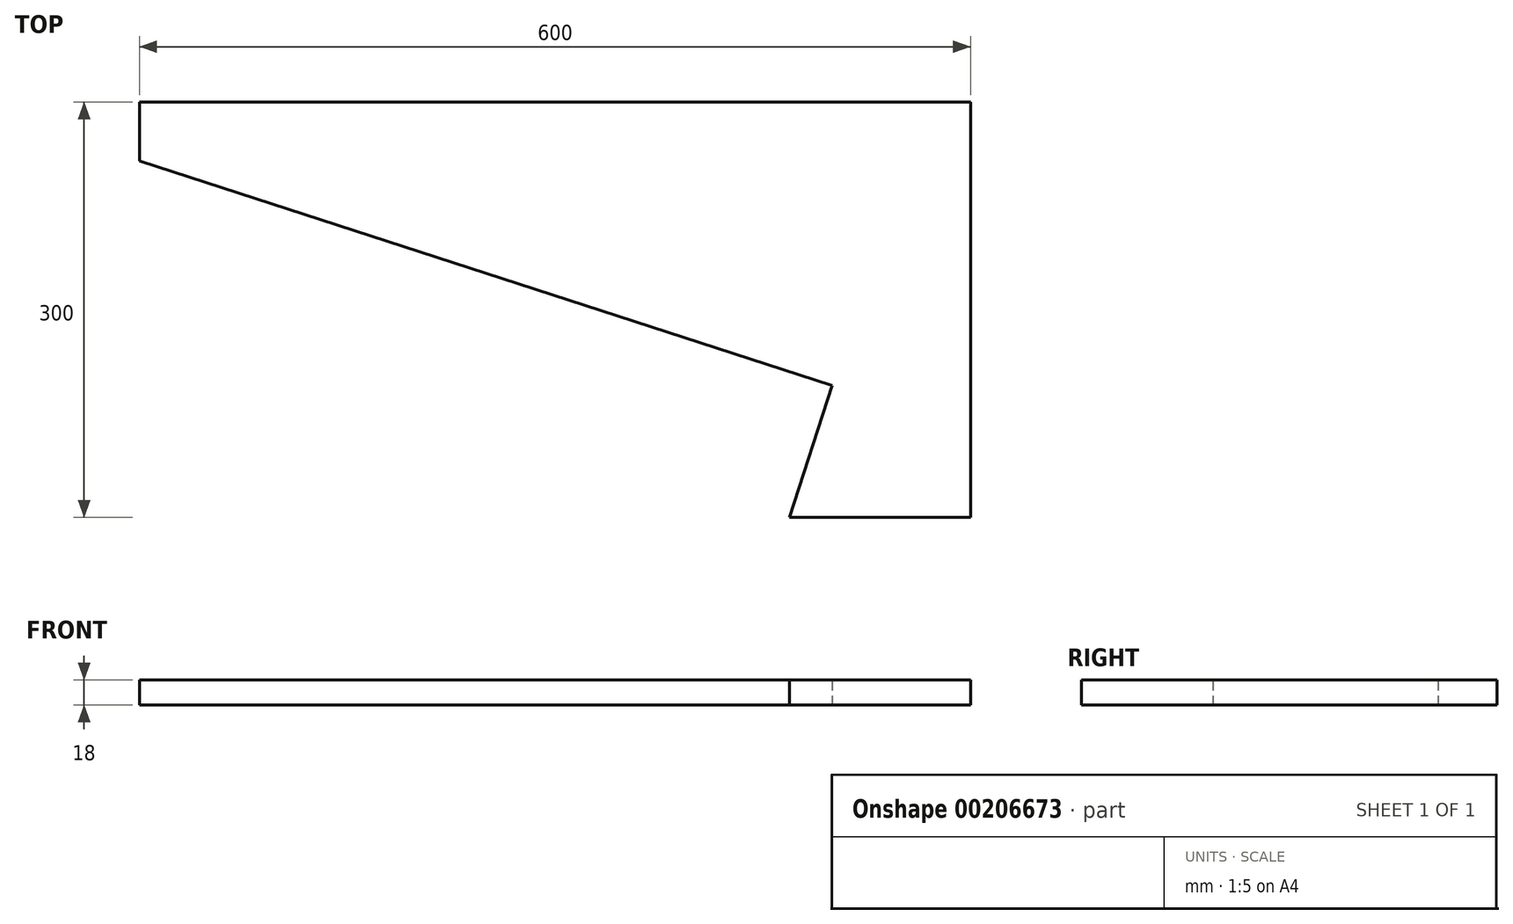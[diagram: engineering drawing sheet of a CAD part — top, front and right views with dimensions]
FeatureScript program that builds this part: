
annotation { "Feature Type Name" : "Feature", "Feature Type Description" : "" }
export const myFeature = defineFeature(function(context is Context, id is Id, definition is map)
    precondition{}
    {
        {
            var Q0;
            Q0=qCreatedBy(makeId("Top.planeOp"),FACE);
            var sketch = newSketch(context, id + "F0", { "sketchPlane" : qUnion([Q0])});
            skLineSegment(sketch, "E0.bottom", {"start": v(-600, 150) * mm, "end": v(600, 150) * mm, "construction": true});
            skLineSegment(sketch, "E0.top", {"start": v(-600, -150) * mm, "end": v(600, -150) * mm, "construction": true});
            skLineSegment(sketch, "E0.left", {"start": v(-600, 150) * mm, "end": v(-600, -150) * mm, "construction": true});
            skLineSegment(sketch, "E0.right", {"start": v(600, 150) * mm, "end": v(600, -150) * mm, "construction": true});
            skPoint(sketch, "E0.middle", {"position": v(0, 0) * mm});
            skLineSegment(sketch, "E1", {"start": v(-600, 150) * mm, "end": v(0, 150) * mm});
            skLineSegment(sketch, "E2", {"start": v(0, 150) * mm, "end": v(0, -150) * mm});
            skLineSegment(sketch, "E3", {"start": v(0, -150) * mm, "end": v(-130.9, -150) * mm});
            skLineSegment(sketch, "E4", {"start": v(-130.9, -150) * mm, "end": v(-100, -54.9) * mm});
            skLineSegment(sketch, "E5", {"start": v(-100, -54.9) * mm, "end": v(-600, 107.57) * mm});
            skLineSegment(sketch, "E6", {"start": v(-600, 107.57) * mm, "end": v(-600, 150) * mm});
            skLineSegment(sketch, "E7", {"start": v(-600, -150) * mm, "end": v(-314.68, -57.3) * mm});
            skLineSegment(sketch, "E8", {"start": v(-314.68, -57.3) * mm, "end": v(-314.68, 14.86) * mm});
            skLineSegment(sketch, "E9", {"start": v(-314.68, 14.86) * mm, "end": v(-600, 107.57) * mm});
            skLineSegment(sketch, "E10", {"start": v(-600, 107.57) * mm, "end": v(-600, -150) * mm});
            skPoint(sketch, "E11.endSnap0", {"position": v(-314.68, -21.22) * mm});
            skPoint(sketch, "E11.endSnap1", {"position": v(-600, -21.22) * mm});
            skLineSegment(sketch, "E12", {"start": v(-314.68, -21.22) * mm, "end": v(-600, -21.22) * mm, "construction": true});
            skLineSegment(sketch, "E13", {"start": v(600, 107.57) * mm, "end": v(100, -54.9) * mm});
            skLineSegment(sketch, "E14", {"start": v(100, -54.9) * mm, "end": v(130.9, -150) * mm});
            skLineSegment(sketch, "E15", {"start": v(130.9, -150) * mm, "end": v(0, -150) * mm});
            skLineSegment(sketch, "E16", {"start": v(600, 150) * mm, "end": v(600, 107.57) * mm});
            skLineSegment(sketch, "E17", {"start": v(0, -150) * mm, "end": v(0, -200) * mm});
            skLineSegment(sketch, "E18", {"start": v(0, -200) * mm, "end": v(-210.24, -200) * mm});
            skLineSegment(sketch, "E19", {"start": v(-210.24, -200) * mm, "end": v(-187.97, -131.46) * mm});
            skLineSegment(sketch, "E20", {"start": v(-187.97, -131.46) * mm, "end": v(-130.9, -150) * mm});
            skLineSegment(sketch, "E21", {"start": v(-130.9, -150) * mm, "end": v(0, -150) * mm});
            skSolve(sketch);
        }
        {
            var Q0;
            Q0=makeQuery(id+"F0.imprint","IMPRINT",FACE,{"disambiguationData":[TD([[makeQuery(id+"F0.imprint","IMPRINT",EDGE,{"derivedFrom":sQuery(id+"F0.wireOp",EDGE,"E1")}),-1.0]])]});
            extrude(context, id + "F1", {"entities" : qUnion([Q0]), "depth" : 18 * mm});
        }
    });
